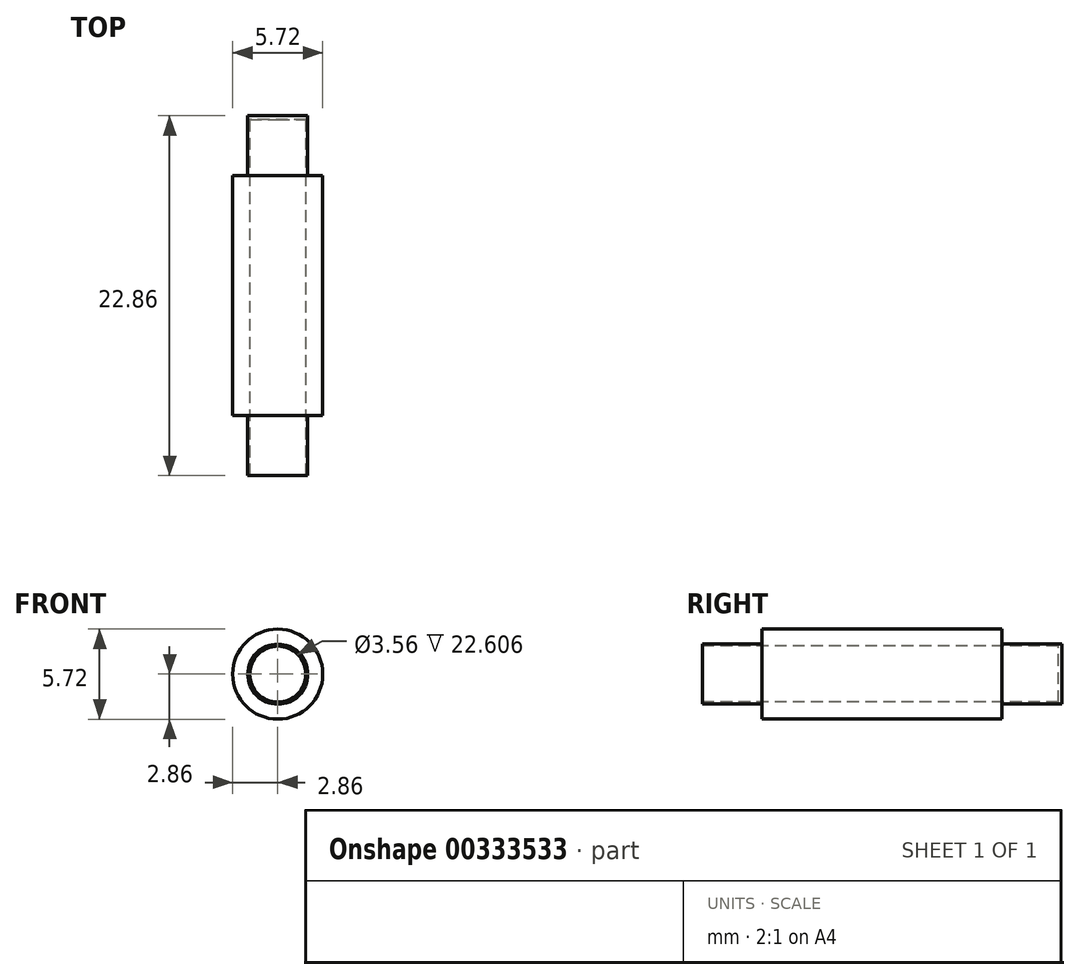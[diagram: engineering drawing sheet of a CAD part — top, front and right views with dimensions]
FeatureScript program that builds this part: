
annotation { "Feature Type Name" : "Feature", "Feature Type Description" : "" }
export const myFeature = defineFeature(function(context is Context, id is Id, definition is map)
    precondition{}
    {
        {
            var Q0;
            Q0=qCreatedBy(makeId("Front.planeOp"),FACE);
            var sketch = newSketch(context, id + "F0", { "sketchPlane" : qUnion([Q0])});
            skCircle(sketch, "E0", {"center": v(0, 0) * mm, "radius": 2.86 * mm});
            skSolve(sketch);
        }
        {
            var Q0;
            Q0 = qSketchRegion(id + "F0", true);
            extrude(context, id + "F1", {"entities" : qUnion([Q0]), "depth" : 15.24 * mm, "offsetDistance" : 25.4 * mm, "symmetric" : true});
        }
        {
            var Q0;
            Q0=qCreatedBy(makeId("Front.planeOp"),FACE);
            var sketch = newSketch(context, id + "F2", { "sketchPlane" : qUnion([Q0])});
            skCircle(sketch, "E1", {"center": v(0, 0) * mm, "radius": 1.9 * mm});
            skSolve(sketch);
        }
        {
            var Q0;
            Q0 = qSketchRegion(id + "F2", true);
            extrude(context, id + "F3", {"entities" : qUnion([Q0]), "operationType" : NewBodyOperationType.ADD, "depth" : 22.86 * mm, "offsetDistance" : 25.4 * mm, "symmetric" : true});
        }
        {
            var Q0;
            Q0=makeQuery(id+"F3.opExtrude","CAP_FACE",FACE,{"disambiguationData":[OSD([sQuery(id+"F2.wireOp",EDGE,"E1")])],"isStart":false});
            var sketch = newSketch(context, id + "F4", { "sketchPlane" : qUnion([Q0])});
            skCircle(sketch, "E2", {"center": v(0, 0) * mm, "radius": 1.78 * mm});
            skSolve(sketch);
        }
        {
            var Q0;
            Q0 = qSketchRegion(id + "F4", true);
            extrude(context, id + "F5", {"entities" : qUnion([Q0]), "operationType" : NewBodyOperationType.REMOVE, "oppositeDirection" : true, "depth" : 22.6 * mm, "offsetDistance" : 25.4 * mm});
        }
    });
